# Revit family: GRIFO DE BIDET KILY con desagüe automatico
name_source: partatom
category: Aparatos sanitarios
revit_build: Autodesk Revit 2015 (Build: 20140223_1515(x64)
units: mm (PartAtom-declared; Revit-internal decimal feet)

## types (1)
- 4956000
    Accionamiento = Por maneta
    CAUDAL = 11,4 l/min a 3 bar
    Comentarios de tipo = ◦Grifo monomando de bidet
◦Acabado Cromo
◦Sin desagüe automático
◦Cartucho sellado mezclador con discos cerámicos Ø25mm y aireador oculto
◦Tubos de alimentación flexibles 3/8" y longitud 45 cm.
    Conexión AC = Sí
    Conexión AF = Sí
    Código de montaje = C1030220
    Descripción = Grifo monomando de bidet Kily. Colección de líneas refinadas y elegantes que se adaptan a todo tipo de ambientes. Su original maneta de forma ondulada destaca en inclinación del escultural diseño del cuerpo del grifo. Una grifería que decora el espacio de baño con personalidad siendo piezas prácticas y ergonómicas muy confortables con el toque de distinción perfecto.
    ENTRADA = Con latiguillos flexibles de 3/8”
    Elevación por defecto = 1219 mm
    Fabricante = PRESTO IBÉRICA
    Imagen de tipo = <Ninguno>
    Material = LATON CROMADO
    Modelo = KILY
    REFERENCIA = 4956000
    TIPO DE AGUA = Fria/Caliene
    Teléfono = (+34) 915 782 575
    URL = http://www.griferiasgalindo.com
